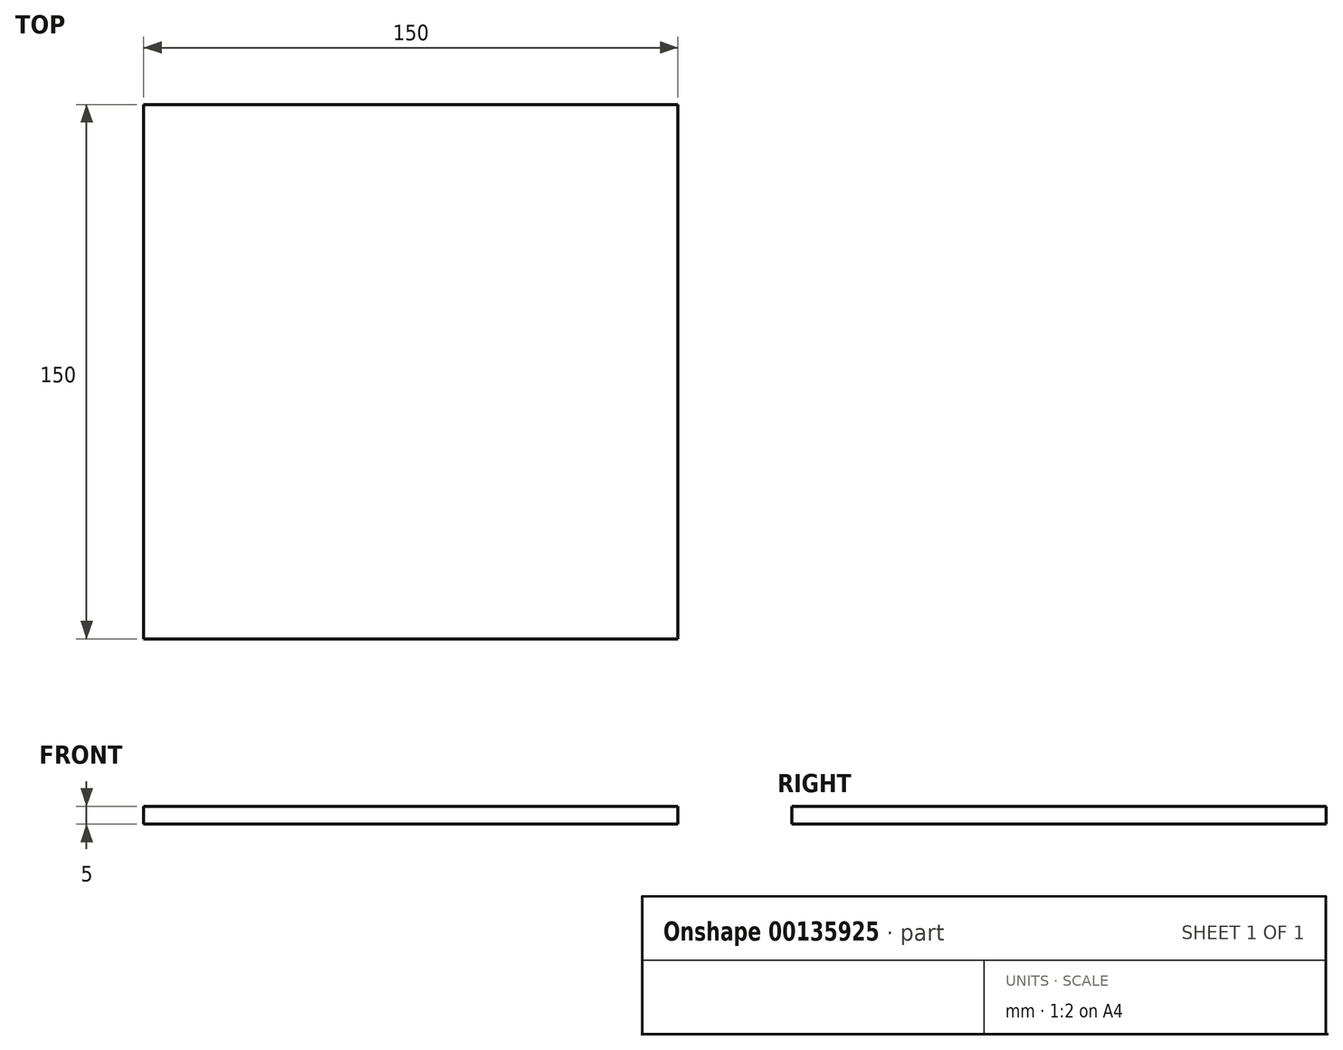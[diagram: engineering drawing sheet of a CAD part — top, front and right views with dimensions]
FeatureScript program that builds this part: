
annotation { "Feature Type Name" : "Feature", "Feature Type Description" : "" }
export const myFeature = defineFeature(function(context is Context, id is Id, definition is map)
    precondition{}
    {
        {
            var Q0;
            Q0=qCreatedBy(makeId("Top.planeOp"),FACE);
            var sketch = newSketch(context, id + "F0", { "sketchPlane" : qUnion([Q0])});
            skLineSegment(sketch, "E0.rect.bottom", {"start": v(75, 75) * mm, "end": v(-75, 75) * mm});
            skLineSegment(sketch, "E0.rect.top", {"start": v(75, -75) * mm, "end": v(-75, -75) * mm});
            skLineSegment(sketch, "E0.rect.left", {"start": v(75, 75) * mm, "end": v(75, -75) * mm});
            skLineSegment(sketch, "E0.rect.right", {"start": v(-75, 75) * mm, "end": v(-75, -75) * mm});
            skPoint(sketch, "E0.rect.middle", {"position": v(0, 0) * mm});
            skSolve(sketch);
        }
        {
            var Q0;
            Q0=qSketchRegion(id+"F0",true);
            extrude(context, id + "F1", {"entities" : qUnion([Q0]), "depth" : 5 * mm});
        }
    });
